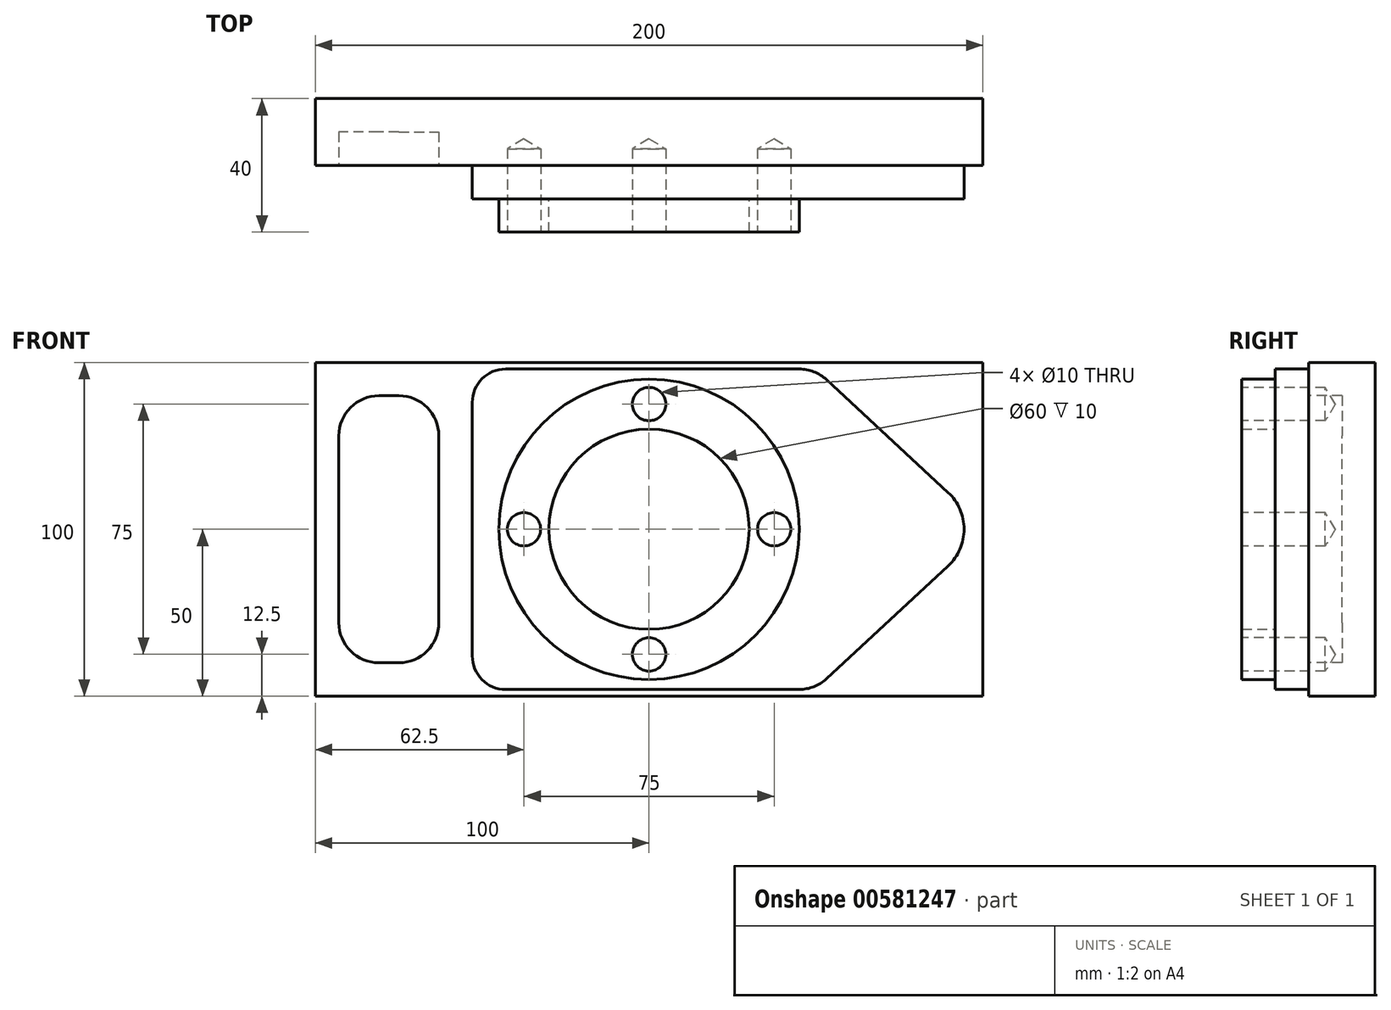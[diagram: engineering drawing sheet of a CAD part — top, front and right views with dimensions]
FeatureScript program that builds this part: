
annotation { "Feature Type Name" : "Feature", "Feature Type Description" : "" }
export const myFeature = defineFeature(function(context is Context, id is Id, definition is map)
    precondition{}
    {
        {
            var Q0;
            Q0=qCreatedBy(makeId("Front.planeOp"),FACE);
            var sketch = newSketch(context, id + "F0", { "sketchPlane" : qUnion([Q0])});
            skLineSegment(sketch, "E0.bottom", {"start": v(100, -50) * mm, "end": v(-100, -50) * mm});
            skLineSegment(sketch, "E0.top", {"start": v(100, 50) * mm, "end": v(-100, 50) * mm});
            skLineSegment(sketch, "E0.left", {"start": v(100, -50) * mm, "end": v(100, 50) * mm});
            skLineSegment(sketch, "E0.right", {"start": v(-100, -50) * mm, "end": v(-100, 50) * mm});
            skPoint(sketch, "E0.middle", {"position": v(0, 0) * mm});
            skSolve(sketch);
        }
        {
            var Q0;
            Q0=makeQuery(id+"F0.imprint","IMPRINT",FACE,{"disambiguationData":[TD([[makeQuery(id+"F0.imprint","IMPRINT",EDGE,{"derivedFrom":sQuery(id+"F0.wireOp",EDGE,"E0.bottom")}),-1.0]])]});
            extrude(context, id + "F1", {"entities" : qUnion([Q0]), "depth" : 20 * mm, "offsetDistance" : 25 * mm});
        }
        {
            var Q0;
            Q0=makeQuery(id+"F1.opExtrude","CAP_FACE",FACE,{"disambiguationData":[OSD([sQuery(id+"F0.wireOp",EDGE,"E0.bottom"),sQuery(id+"F0.wireOp",EDGE,"E0.top"),sQuery(id+"F0.wireOp",EDGE,"E0.left"),sQuery(id+"F0.wireOp",EDGE,"E0.right")])],"isStart":false});
            var sketch = newSketch(context, id + "F2", { "sketchPlane" : qUnion([Q0])});
            skLineSegment(sketch, "E1.bottom", {"start": v(-75, -40) * mm, "end": v(-81, -40) * mm});
            skLineSegment(sketch, "E1.top", {"start": v(-75, 40) * mm, "end": v(-81, 40) * mm});
            skLineSegment(sketch, "E1.left", {"start": v(-63, -28) * mm, "end": v(-63, 28) * mm});
            skLineSegment(sketch, "E1.right", {"start": v(-93, -28) * mm, "end": v(-93, 28) * mm});
            skPoint(sketch, "E1.middle", {"position": v(-78, 0) * mm});
            skPoint(sketch, "E2.visualSharp", {"position": v(-93, 40) * mm});
            skArc(sketch, "E2.filletArc", {"start": v(-81, 40) * mm, "mid": v(-89.49, 36.49) * mm, "end": v(-93, 28) * mm});
            skPoint(sketch, "E3.visualSharp", {"position": v(-63, 40) * mm});
            skArc(sketch, "E3.filletArc", {"start": v(-63, 28) * mm, "mid": v(-66.51, 36.49) * mm, "end": v(-75, 40) * mm});
            skPoint(sketch, "E4.visualSharp", {"position": v(-93, -40) * mm});
            skArc(sketch, "E4.filletArc", {"start": v(-93, -28) * mm, "mid": v(-89.49, -36.49) * mm, "end": v(-81, -40) * mm});
            skPoint(sketch, "E5.visualSharp", {"position": v(-63, -40) * mm});
            skArc(sketch, "E5.filletArc", {"start": v(-75, -40) * mm, "mid": v(-66.51, -36.49) * mm, "end": v(-63, -28) * mm});
            skSolve(sketch);
        }
        {
            var Q0;
            Q0=makeQuery(id+"F2.imprint","IMPRINT",FACE,{"disambiguationData":[TD([[makeQuery(id+"F2.imprint","IMPRINT",EDGE,{"derivedFrom":sQuery(id+"F2.wireOp",EDGE,"E1.bottom")}),-1.0]])]});
            extrude(context, id + "F3", {"entities" : qUnion([Q0]), "operationType" : NewBodyOperationType.REMOVE, "oppositeDirection" : true, "depth" : 10 * mm, "offsetDistance" : 25 * mm});
        }
        {
            var Q0;
            Q0=makeQuery(id+"F1.opExtrude","CAP_FACE",FACE,{"disambiguationData":[OSD([sQuery(id+"F0.wireOp",EDGE,"E0.bottom"),sQuery(id+"F0.wireOp",EDGE,"E0.top"),sQuery(id+"F0.wireOp",EDGE,"E0.left"),sQuery(id+"F0.wireOp",EDGE,"E0.right")])],"isStart":false});
            var sketch = newSketch(context, id + "F4", { "sketchPlane" : qUnion([Q0])});
            skPoint(sketch, "E6.middle", {"position": v(0, 0) * mm});
            skLineSegment(sketch, "E7", {"start": v(-53, 38) * mm, "end": v(-53, -38) * mm});
            skLineSegment(sketch, "E8", {"start": v(-43, 48) * mm, "end": v(45, 48) * mm});
            skArc(sketch, "E9", {"start": v(-43, 48) * mm, "mid": v(-50.07, 45.07) * mm, "end": v(-53, 38) * mm});
            skLineSegment(sketch, "E10", {"start": v(-43, -48) * mm, "end": v(45, -48) * mm});
            skArc(sketch, "E11", {"start": v(-53, -38) * mm, "mid": v(-50.07, -45.07) * mm, "end": v(-43, -48) * mm});
            skLineSegment(sketch, "E12", {"start": v(53.16, 44.8) * mm, "end": v(89.62, 11) * mm});
            skLineSegment(sketch, "E13", {"start": v(53.16, -44.8) * mm, "end": v(89.62, -11) * mm});
            skArc(sketch, "E14", {"start": v(53.16, 44.8) * mm, "mid": v(49.38, 47.17) * mm, "end": v(45, 48) * mm});
            skArc(sketch, "E15", {"start": v(45, -48) * mm, "mid": v(49.38, -47.17) * mm, "end": v(53.16, -44.8) * mm});
            skArc(sketch, "E16", {"start": v(89.62, -11) * mm, "mid": v(94.42, 0) * mm, "end": v(89.62, 11) * mm});
            skSolve(sketch);
        }
        {
            var Q0;
            Q0=makeQuery(id+"F4.imprint","IMPRINT",FACE,{"disambiguationData":[TD([[makeQuery(id+"F4.imprint","IMPRINT",EDGE,{"derivedFrom":sQuery(id+"F4.wireOp",EDGE,"E7")}),1.0]])]});
            extrude(context, id + "F5", {"entities" : qUnion([Q0]), "operationType" : NewBodyOperationType.ADD, "depth" : 10 * mm, "offsetDistance" : 25 * mm});
        }
        {
            var Q0;
            Q0=makeQuery(id+"F5.opExtrude","CAP_FACE",FACE,{"disambiguationData":[OSD([sQuery(id+"F4.wireOp",EDGE,"E7"),sQuery(id+"F4.wireOp",EDGE,"E8"),sQuery(id+"F4.wireOp",EDGE,"E9"),sQuery(id+"F4.wireOp",EDGE,"E10"),sQuery(id+"F4.wireOp",EDGE,"E11"),sQuery(id+"F4.wireOp",EDGE,"E12"),sQuery(id+"F4.wireOp",EDGE,"E13"),sQuery(id+"F4.wireOp",EDGE,"E14"),sQuery(id+"F4.wireOp",EDGE,"E15"),sQuery(id+"F4.wireOp",EDGE,"E16")])],"isStart":false});
            var sketch = newSketch(context, id + "F6", { "sketchPlane" : qUnion([Q0])});
            skCircle(sketch, "E17", {"center": v(0, 0) * mm, "radius": 45 * mm});
            skCircle(sketch, "E18", {"center": v(0, 0) * mm, "radius": 30 * mm});
            skSolve(sketch);
        }
        {
            var Q0;
            Q0=makeQuery(id+"F6.imprint","IMPRINT",FACE,{"disambiguationData":[TD([[makeQuery(id+"F6.imprint","IMPRINT",EDGE,{"derivedFrom":sQuery(id+"F6.wireOp",EDGE,"E17")}),1.0]])]});
            extrude(context, id + "F7", {"entities" : qUnion([Q0]), "operationType" : NewBodyOperationType.ADD, "depth" : 10 * mm, "offsetDistance" : 25 * mm});
        }
        {
            var Q0;
            Q0=makeQuery(id+"F7.opExtrude","CAP_FACE",FACE,{"disambiguationData":[OSD([sQuery(id+"F6.wireOp",EDGE,"E17"),sQuery(id+"F6.wireOp",EDGE,"E18")])],"isStart":false});
            var sketch = newSketch(context, id + "F8", { "sketchPlane" : qUnion([Q0])});
            skCircle(sketch, "E19", {"center": v(0, 0) * mm, "radius": 37.5 * mm, "construction": true});
            skCircle(sketch, "E20", {"center": v(0, 37.5) * mm, "radius": 5 * mm});
            skCircle(sketch, "E21", {"center": v(0, -37.5) * mm, "radius": 5 * mm});
            skCircle(sketch, "E22", {"center": v(-37.5, 0) * mm, "radius": 5 * mm});
            skCircle(sketch, "E23", {"center": v(37.5, 0) * mm, "radius": 5 * mm});
            skSolve(sketch);
        }
        {
            var Q0;
            Q0=sQuery(id+"F8.wireOp",VERTEX,"E22.center");
            var Q1;
            Q1=sQuery(id+"F8.wireOp",VERTEX,"E20.center");
            var Q2;
            Q2=sQuery(id+"F8.wireOp",VERTEX,"E23.center");
            var Q3;
            Q3=sQuery(id+"F8.wireOp",VERTEX,"E21.center");
            var Q4;
            Q4=makeQuery(id+"F1.opExtrude","SWEPT_BODY",BODY,{"disambiguationData":[OSD([sQuery(id+"F0.wireOp",EDGE,"E0.bottom"),sQuery(id+"F0.wireOp",EDGE,"E0.top"),sQuery(id+"F0.wireOp",EDGE,"E0.left"),sQuery(id+"F0.wireOp",EDGE,"E0.right")])]});
            hole(context, id + "F9", {"style" : HoleStyle.SIMPLE, "endStyle" : HoleEndStyle.BLIND, "holeDiameter" : 10 * mm, "majorDiameter" : 5 * mm, "holeDepth" : 25 * mm, "isTappedThrough" : true, "tappedDepth" : 12 * mm, "tapClearance" : 3, "locations" : qUnion([Q0, Q1, Q2, Q3]), "scope" : qUnion([Q4])});
        }
    });
